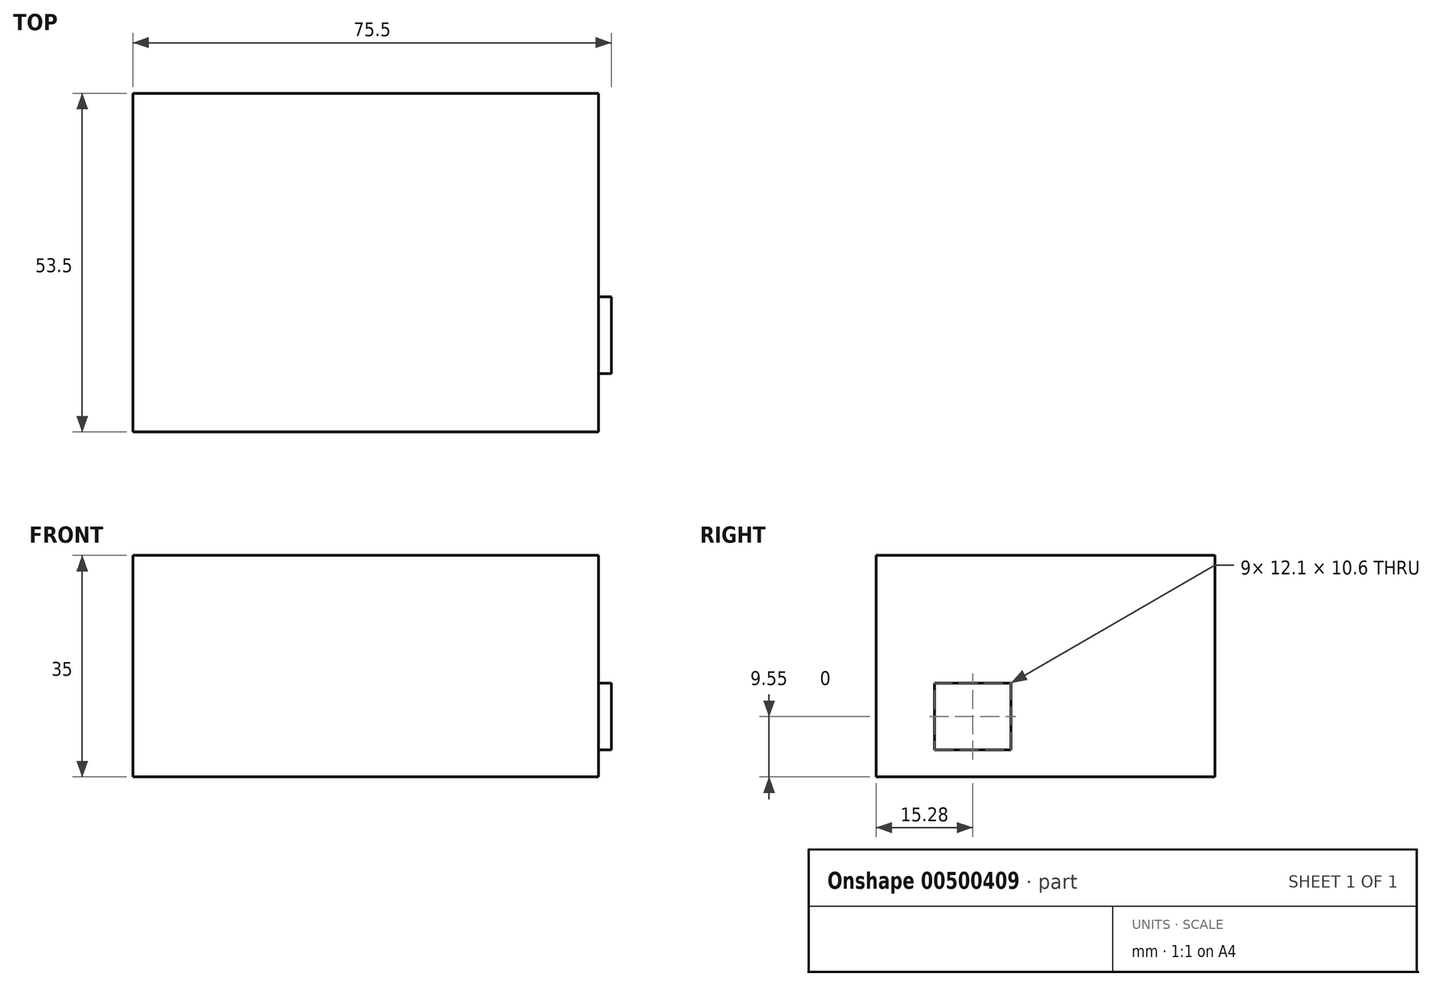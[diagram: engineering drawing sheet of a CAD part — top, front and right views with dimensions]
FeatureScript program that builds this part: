
annotation { "Feature Type Name" : "Feature", "Feature Type Description" : "" }
export const myFeature = defineFeature(function(context is Context, id is Id, definition is map)
    precondition{}
    {
        {
            var Q0;
            Q0=qCreatedBy(makeId("Top.planeOp"),FACE);
            var sketch = newSketch(context, id + "F0", { "sketchPlane" : qUnion([Q0])});
            skLineSegment(sketch, "E0.bottom", {"start": v(37.75, -26.75) * mm, "end": v(-37.75, -26.75) * mm});
            skLineSegment(sketch, "E0.top", {"start": v(37.75, 26.75) * mm, "end": v(-37.75, 26.75) * mm});
            skLineSegment(sketch, "E0.left", {"start": v(37.75, -26.75) * mm, "end": v(37.75, 26.75) * mm});
            skLineSegment(sketch, "E0.right", {"start": v(-37.75, -26.75) * mm, "end": v(-37.75, 26.75) * mm});
            skPoint(sketch, "E0.middle", {"position": v(0, 0) * mm});
            skSolve(sketch);
        }
        {
            var Q0;
            Q0=makeQuery(id+"F0.imprint","IMPRINT",FACE,{"disambiguationData":[TD([[makeQuery(id+"F0.imprint","IMPRINT",EDGE,{"derivedFrom":sQuery(id+"F0.wireOp",EDGE,"E0.bottom")}),-1.0]])]});
            extrude(context, id + "F1", {"entities" : qUnion([Q0]), "depth" : 35 * mm});
        }
        {
            var Q0;
            Q0=makeQuery(id+"F1.opExtrude","SWEPT_FACE",FACE,{"disambiguationData":[OSD([sQuery(id+"F0.wireOp",EDGE,"E0.left")])]});
            var sketch = newSketch(context, id + "F2", { "sketchPlane" : qUnion([Q0])});
            skLineSegment(sketch, "E1", {"start": v(-26.75, 11.1) * mm, "end": v(-17.52, 11.1) * mm, "construction": true});
            skLineSegment(sketch, "E2", {"start": v(-13.98, 0) * mm, "end": v(-13.98, 4.25) * mm, "construction": true});
            skLineSegment(sketch, "E3.bottom", {"start": v(-17.52, 4.25) * mm, "end": v(-5.42, 4.25) * mm});
            skLineSegment(sketch, "E3.top", {"start": v(-17.52, 14.85) * mm, "end": v(-5.42, 14.85) * mm});
            skLineSegment(sketch, "E3.left", {"start": v(-17.52, 4.25) * mm, "end": v(-17.52, 14.85) * mm});
            skLineSegment(sketch, "E3.right", {"start": v(-5.42, 4.25) * mm, "end": v(-5.42, 14.85) * mm});
            skSolve(sketch);
        }
        {
            var Q0;
            Q0=makeQuery(id+"F2.imprint","IMPRINT",FACE,{"disambiguationData":[TD([[makeQuery(id+"F2.imprint","IMPRINT",EDGE,{"derivedFrom":sQuery(id+"F2.wireOp",EDGE,"E3.bottom")}),-1.0]])]});
            extrude(context, id + "F3", {"entities" : qUnion([Q0]), "operationType" : NewBodyOperationType.REMOVE, "oppositeDirection" : true, "depth" : 2 * mm});
        }
    });
